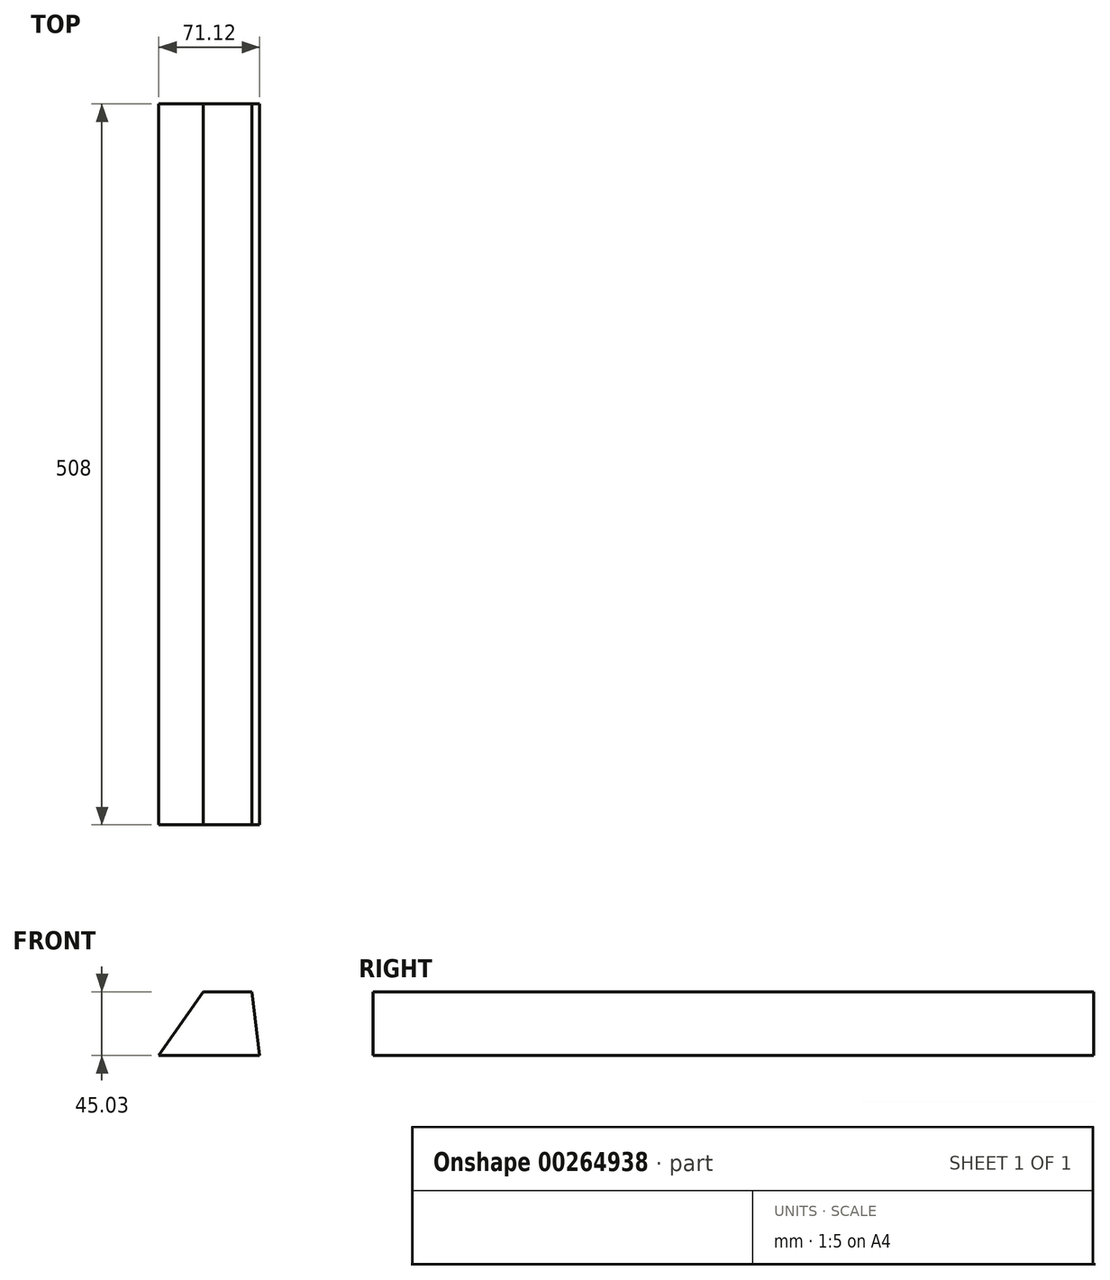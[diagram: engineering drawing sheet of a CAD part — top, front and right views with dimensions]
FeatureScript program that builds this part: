
annotation { "Feature Type Name" : "Feature", "Feature Type Description" : "" }
export const myFeature = defineFeature(function(context is Context, id is Id, definition is map)
    precondition{}
    {
        {
            var Q0;
            Q0=qCreatedBy(makeId("Front.planeOp"),FACE);
            var sketch = newSketch(context, id + "F0", { "sketchPlane" : qUnion([Q0])});
            skLineSegment(sketch, "E0", {"start": v(0, 0) * mm, "end": v(-71.12, 0) * mm});
            skLineSegment(sketch, "E1", {"start": v(-71.12, 0) * mm, "end": v(-39.86, 45.03) * mm});
            skLineSegment(sketch, "E2", {"start": v(-39.86, 45.03) * mm, "end": v(-5.54, 45.03) * mm});
            skLineSegment(sketch, "E3", {"start": v(-5.54, 45.03) * mm, "end": v(0, 0) * mm});
            skSolve(sketch);
        }
        {
            var Q0;
            Q0 = qSketchRegion(id + "F0", true);
            extrude(context, id + "F1", {"entities" : qUnion([Q0]), "depth" : 508 * mm});
        }
    });
